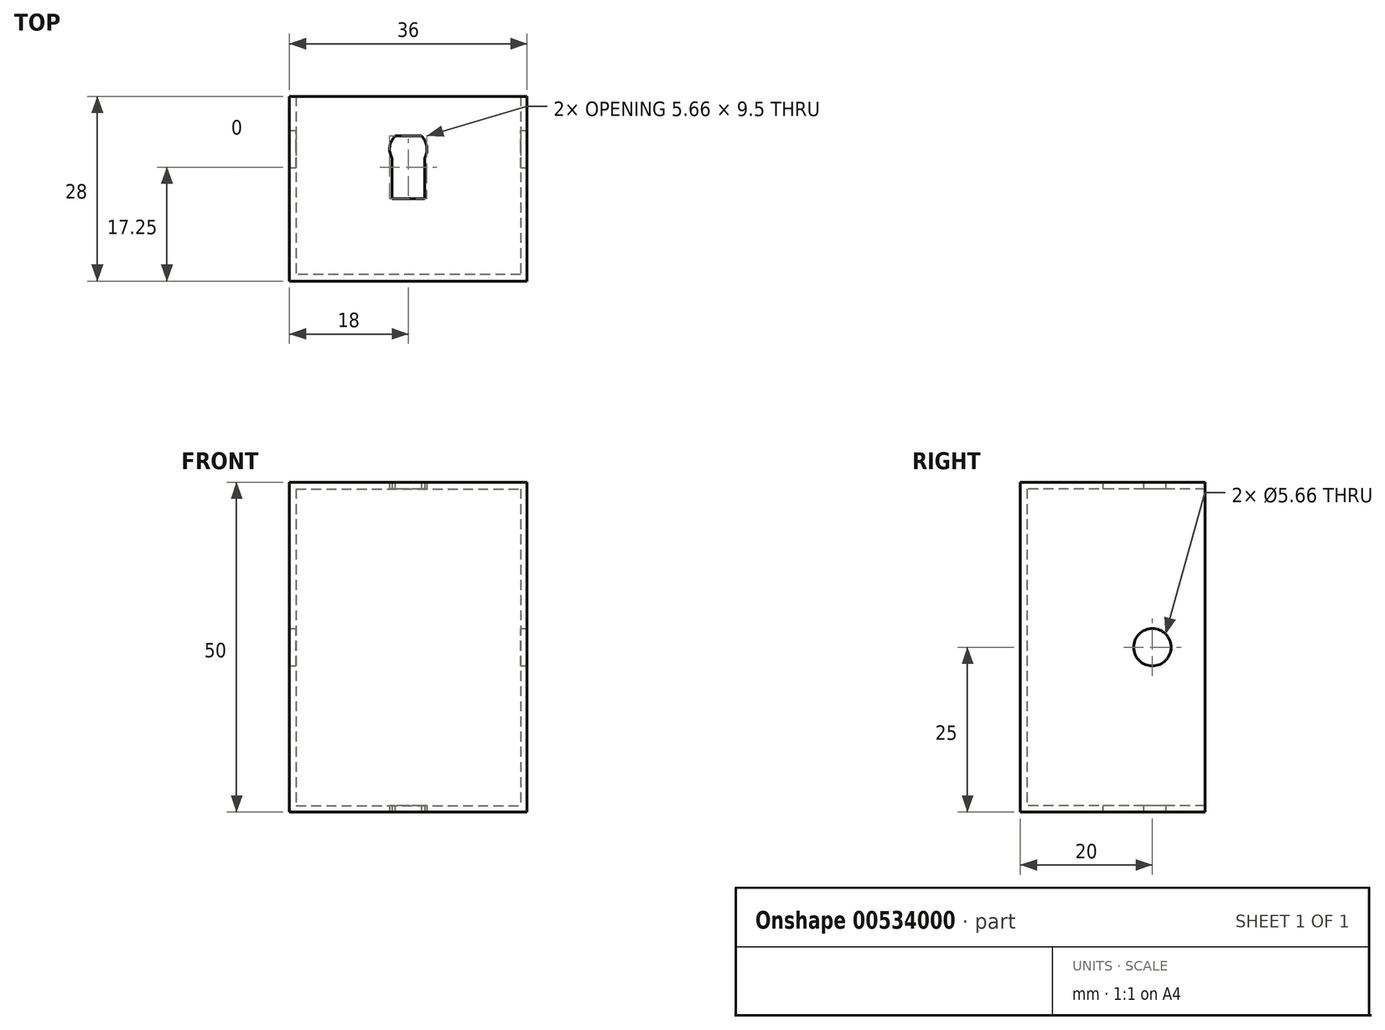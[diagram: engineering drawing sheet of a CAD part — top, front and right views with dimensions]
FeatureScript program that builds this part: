
annotation { "Feature Type Name" : "Feature", "Feature Type Description" : "" }
export const myFeature = defineFeature(function(context is Context, id is Id, definition is map)
    precondition{}
    {
        {
            var Q0;
            Q0=qCreatedBy(makeId("Top.planeOp"),FACE);
            var sketch = newSketch(context, id + "F0", { "sketchPlane" : qUnion([Q0])});
            skCircle(sketch, "E0", {"center": v(0, 0) * mm, "radius": 15 * mm});
            skLineSegment(sketch, "E1", {"start": v(0, 15) * mm, "end": v(0, -15) * mm});
            skLineSegment(sketch, "E2.bottom", {"start": v(2.5, 7.5) * mm, "end": v(-2.5, 7.5) * mm});
            skLineSegment(sketch, "E2.top", {"start": v(2.5, -7.5) * mm, "end": v(-2.5, -7.5) * mm});
            skLineSegment(sketch, "E2.left", {"start": v(2.5, 7.5) * mm, "end": v(2.5, -7.5) * mm});
            skLineSegment(sketch, "E2.right", {"start": v(-2.5, 7.5) * mm, "end": v(-2.5, -7.5) * mm});
            skLineSegment(sketch, "E3.bottom", {"start": v(6, 15.5) * mm, "end": v(-6, 15.5) * mm});
            skLineSegment(sketch, "E3.top", {"start": v(6, 8.5) * mm, "end": v(-6, 8.5) * mm});
            skLineSegment(sketch, "E3.left", {"start": v(6, 15.5) * mm, "end": v(6, 8.5) * mm});
            skLineSegment(sketch, "E3.right", {"start": v(-6, 15.5) * mm, "end": v(-6, 8.5) * mm});
            skPoint(sketch, "E3.middle", {"position": v(0, 12) * mm});
            skLineSegment(sketch, "E4.bottom", {"start": v(17, 19) * mm, "end": v(-17, 19) * mm});
            skLineSegment(sketch, "E4.top", {"start": v(17, -19) * mm, "end": v(-17, -19) * mm});
            skLineSegment(sketch, "E4.left", {"start": v(17, 19) * mm, "end": v(17, -19) * mm});
            skLineSegment(sketch, "E4.right", {"start": v(-17, 19) * mm, "end": v(-17, -19) * mm});
            skLineSegment(sketch, "E5.0", {"start": v(18, 20) * mm, "end": v(-18, 20) * mm});
            skLineSegment(sketch, "E5.1", {"start": v(18, 20) * mm, "end": v(18, -20) * mm});
            skLineSegment(sketch, "E5.2", {"start": v(18, -20) * mm, "end": v(-18, -20) * mm});
            skLineSegment(sketch, "E5.3", {"start": v(-18, 20) * mm, "end": v(-18, -20) * mm});
            skLineSegment(sketch, "E6", {"start": v(-18, 8) * mm, "end": v(18, 8) * mm});
            skLineSegment(sketch, "E7", {"start": v(18, 8) * mm, "end": v(17, 8) * mm});
            skLineSegment(sketch, "E8", {"start": v(-18, 8) * mm, "end": v(-17, 8) * mm});
            skCircle(sketch, "E9", {"center": v(0, 0) * mm, "radius": 17 * mm});
            skLineSegment(sketch, "E10.bottom", {"start": v(2, 2) * mm, "end": v(-2, 2) * mm});
            skLineSegment(sketch, "E10.top", {"start": v(2, -2) * mm, "end": v(-2, -2) * mm});
            skLineSegment(sketch, "E10.left", {"start": v(2, 2) * mm, "end": v(2, -2) * mm});
            skLineSegment(sketch, "E10.right", {"start": v(-2, 2) * mm, "end": v(-2, -2) * mm});
            skCircle(sketch, "E11", {"center": v(0, 0) * mm, "radius": 2.83 * mm});
            skLineSegment(sketch, "E12", {"start": v(2, 0) * mm, "end": v(-2, 0) * mm});
            skLineSegment(sketch, "E13", {"start": v(-18, 0) * mm, "end": v(18, 0) * mm, "construction": true});
            skSolve(sketch);
        }
        {
            var Q0;
            Q0=qCreatedBy(makeId("Right.planeOp"),FACE);
            var sketch = newSketch(context, id + "F1", { "sketchPlane" : qUnion([Q0])});
            skLineSegment(sketch, "E14.bottom", {"start": v(2, 2) * mm, "end": v(-2, 2) * mm});
            skLineSegment(sketch, "E14.top", {"start": v(2, -2) * mm, "end": v(-2, -2) * mm});
            skLineSegment(sketch, "E14.left", {"start": v(2, 2) * mm, "end": v(2, -2) * mm});
            skLineSegment(sketch, "E14.right", {"start": v(-2, 2) * mm, "end": v(-2, -2) * mm});
            skPoint(sketch, "E14.middle", {"position": v(0, 0) * mm});
            skCircle(sketch, "E15", {"center": v(0, 0) * mm, "radius": 2.83 * mm});
            skSolve(sketch);
        }
        {
            var Q0;
            {var subQ1=sQuery(id+"F0.wireOp",EDGE,"E4.top");Q0=makeQuery(id+"F0.imprint","IMPRINT",FACE,{"disambiguationData":[TD([[makeQuery(id+"F0.imprint","IMPRINT",EDGE,{"derivedFrom":subQ1}),1.0]])]});}
            extrude(context, id + "F2", {"entities" : qUnion([Q0]), "depth" : 25 * mm, "offsetDistance" : 25 * mm, "hasSecondDirection" : true, "secondDirectionOppositeDirection" : true, "secondDirectionDepth" : 25 * mm});
        }
        {
            var Q0;
            {var subQ1=sQuery(id+"F0.wireOp",EDGE,"E4.top");Q0=makeQuery(id+"F0.imprint","IMPRINT",FACE,{"disambiguationData":[TD([[makeQuery(id+"F0.imprint","IMPRINT",EDGE,{"derivedFrom":subQ1}),-1.0]])]});}
            var Q1;
            {var subQ1=sQuery(id+"F0.wireOp",EDGE,"E0");var subQ5=makeQuery(id+"F0.imprint","INTERSECT",VERTEX,{"disambiguationData":[OD(1.0)],"derivedFrom":[subQ1,sQuery(id+"F0.wireOp",EDGE,"E1")]});Q1=makeQuery(id+"F0.imprint","IMPRINT",FACE,{"disambiguationData":[TD([[makeQuery(id+"F0.imprint","IMPRINT",EDGE,{"disambiguationData":[TD([[subQ5,1.0]])],"derivedFrom":subQ1}),-1.0]])]});}
            var Q2;
            {var subQ0=sQuery(id+"F0.wireOp",EDGE,"E2.right");Q2=makeQuery(id+"F0.imprint","IMPRINT",FACE,{"disambiguationData":[TD([[makeQuery(id+"F0.imprint","IMPRINT",EDGE,{"derivedFrom":subQ0}),-1.0]])]});}
            var Q3;
            {var subQ0=sQuery(id+"F0.wireOp",EDGE,"E2.left");Q3=makeQuery(id+"F0.imprint","IMPRINT",FACE,{"disambiguationData":[TD([[makeQuery(id+"F0.imprint","IMPRINT",EDGE,{"derivedFrom":subQ0}),1.0]])]});}
            var Q4;
            {var subQ1=sQuery(id+"F0.wireOp",EDGE,"E4.right");var subQ3=sQuery(id+"F0.wireOp",EDGE,"E9");var subQ4=makeQuery(id+"F0.imprint","INTERSECT",VERTEX,{"derivedFrom":[subQ1,subQ3]});Q4=makeQuery(id+"F0.imprint","IMPRINT",FACE,{"disambiguationData":[TD([[makeQuery(id+"F0.imprint","IMPRINT",EDGE,{"disambiguationData":[TD([[subQ4,1.0]])],"derivedFrom":subQ3}),-1.0]])]});}
            var Q5;
            {var subQ1=sQuery(id+"F0.wireOp",EDGE,"E4.left");var subQ3=sQuery(id+"F0.wireOp",EDGE,"E9");var subQ4=makeQuery(id+"F0.imprint","INTERSECT",VERTEX,{"derivedFrom":[subQ1,subQ3]});Q5=makeQuery(id+"F0.imprint","IMPRINT",FACE,{"disambiguationData":[TD([[makeQuery(id+"F0.imprint","IMPRINT",EDGE,{"disambiguationData":[TD([[subQ4,-1.0]])],"derivedFrom":subQ3}),-1.0]])]});}
            var Q6;
            {var subQ1=sQuery(id+"F0.wireOp",EDGE,"E2.bottom");var subQ6=sQuery(id+"F0.wireOp",EDGE,"E1");var subQ8=makeQuery(id+"F0.imprint","INTERSECT",VERTEX,{"derivedFrom":[subQ6,subQ1]});Q6=makeQuery(id+"F0.imprint","IMPRINT",FACE,{"disambiguationData":[TD([[makeQuery(id+"F0.imprint","IMPRINT",EDGE,{"disambiguationData":[TD([[subQ8,-1.0]])],"derivedFrom":subQ6}),-1.0]])]});}
            var Q7;
            {var subQ1=sQuery(id+"F0.wireOp",EDGE,"E2.bottom");var subQ3=sQuery(id+"F0.wireOp",EDGE,"E1");var subQ4=makeQuery(id+"F0.imprint","INTERSECT",VERTEX,{"derivedFrom":[subQ3,subQ1]});Q7=makeQuery(id+"F0.imprint","IMPRINT",FACE,{"disambiguationData":[TD([[makeQuery(id+"F0.imprint","IMPRINT",EDGE,{"disambiguationData":[TD([[subQ4,-1.0]])],"derivedFrom":subQ3}),1.0]])]});}
            var Q8;
            {var subQ0=sQuery(id+"F0.wireOp",EDGE,"E11");var subQ2=sQuery(id+"F0.wireOp",EDGE,"E1");var subQ3=makeQuery(id+"F0.imprint","INTERSECT",VERTEX,{"disambiguationData":[OD(1.0)],"derivedFrom":[subQ2,subQ0]});Q8=makeQuery(id+"F0.imprint","IMPRINT",FACE,{"disambiguationData":[TD([[makeQuery(id+"F0.imprint","IMPRINT",EDGE,{"disambiguationData":[TD([[subQ3,-1.0]])],"derivedFrom":subQ2}),1.0]])]});}
            var Q9;
            {var subQ0=sQuery(id+"F0.wireOp",EDGE,"E11");var subQ6=sQuery(id+"F0.wireOp",EDGE,"E1");var subQ7=makeQuery(id+"F0.imprint","INTERSECT",VERTEX,{"disambiguationData":[OD(1.0)],"derivedFrom":[subQ6,subQ0]});Q9=makeQuery(id+"F0.imprint","IMPRINT",FACE,{"disambiguationData":[TD([[makeQuery(id+"F0.imprint","IMPRINT",EDGE,{"disambiguationData":[TD([[subQ7,-1.0]])],"derivedFrom":subQ6}),-1.0]])]});}
            extrude(context, id + "F3", {"entities" : qUnion([Q0, Q1, Q2, Q3, Q4, Q5, Q6, Q7, Q8, Q9]), "operationType" : NewBodyOperationType.ADD, "depth" : 25 * mm, "offsetDistance" : 25 * mm, "hasSecondDirection" : true, "secondDirectionOppositeDirection" : true, "secondDirectionDepth" : 25 * mm});
        }
        {
            var Q0;
            {var subQ1=sQuery(id+"F0.wireOp",EDGE,"E4.top");Q0=makeQuery(id+"F0.imprint","IMPRINT",FACE,{"disambiguationData":[TD([[makeQuery(id+"F0.imprint","IMPRINT",EDGE,{"derivedFrom":subQ1}),-1.0]])]});}
            var Q1;
            {var subQ0=sQuery(id+"F0.wireOp",EDGE,"E2.left");Q1=makeQuery(id+"F0.imprint","IMPRINT",FACE,{"disambiguationData":[TD([[makeQuery(id+"F0.imprint","IMPRINT",EDGE,{"derivedFrom":subQ0}),1.0]])]});}
            var Q2;
            {var subQ1=sQuery(id+"F0.wireOp",EDGE,"E0");var subQ5=makeQuery(id+"F0.imprint","INTERSECT",VERTEX,{"disambiguationData":[OD(1.0)],"derivedFrom":[subQ1,sQuery(id+"F0.wireOp",EDGE,"E1")]});Q2=makeQuery(id+"F0.imprint","IMPRINT",FACE,{"disambiguationData":[TD([[makeQuery(id+"F0.imprint","IMPRINT",EDGE,{"disambiguationData":[TD([[subQ5,1.0]])],"derivedFrom":subQ1}),-1.0]])]});}
            var Q3;
            {var subQ0=sQuery(id+"F0.wireOp",EDGE,"E2.right");Q3=makeQuery(id+"F0.imprint","IMPRINT",FACE,{"disambiguationData":[TD([[makeQuery(id+"F0.imprint","IMPRINT",EDGE,{"derivedFrom":subQ0}),-1.0]])]});}
            var Q4;
            {var subQ1=sQuery(id+"F0.wireOp",EDGE,"E4.right");var subQ3=sQuery(id+"F0.wireOp",EDGE,"E9");var subQ4=makeQuery(id+"F0.imprint","INTERSECT",VERTEX,{"derivedFrom":[subQ1,subQ3]});Q4=makeQuery(id+"F0.imprint","IMPRINT",FACE,{"disambiguationData":[TD([[makeQuery(id+"F0.imprint","IMPRINT",EDGE,{"disambiguationData":[TD([[subQ4,1.0]])],"derivedFrom":subQ3}),-1.0]])]});}
            var Q5;
            {var subQ1=sQuery(id+"F0.wireOp",EDGE,"E4.left");var subQ3=sQuery(id+"F0.wireOp",EDGE,"E9");var subQ4=makeQuery(id+"F0.imprint","INTERSECT",VERTEX,{"derivedFrom":[subQ1,subQ3]});Q5=makeQuery(id+"F0.imprint","IMPRINT",FACE,{"disambiguationData":[TD([[makeQuery(id+"F0.imprint","IMPRINT",EDGE,{"disambiguationData":[TD([[subQ4,-1.0]])],"derivedFrom":subQ3}),-1.0]])]});}
            var Q6;
            {var subQ0=sQuery(id+"F0.wireOp",EDGE,"E11");var subQ6=sQuery(id+"F0.wireOp",EDGE,"E1");var subQ7=makeQuery(id+"F0.imprint","INTERSECT",VERTEX,{"disambiguationData":[OD(1.0)],"derivedFrom":[subQ6,subQ0]});Q6=makeQuery(id+"F0.imprint","IMPRINT",FACE,{"disambiguationData":[TD([[makeQuery(id+"F0.imprint","IMPRINT",EDGE,{"disambiguationData":[TD([[subQ7,-1.0]])],"derivedFrom":subQ6}),-1.0]])]});}
            var Q7;
            {var subQ0=sQuery(id+"F0.wireOp",EDGE,"E11");var subQ2=sQuery(id+"F0.wireOp",EDGE,"E1");var subQ3=makeQuery(id+"F0.imprint","INTERSECT",VERTEX,{"disambiguationData":[OD(1.0)],"derivedFrom":[subQ2,subQ0]});Q7=makeQuery(id+"F0.imprint","IMPRINT",FACE,{"disambiguationData":[TD([[makeQuery(id+"F0.imprint","IMPRINT",EDGE,{"disambiguationData":[TD([[subQ3,-1.0]])],"derivedFrom":subQ2}),1.0]])]});}
            var Q8;
            {var subQ1=sQuery(id+"F0.wireOp",EDGE,"E2.bottom");var subQ6=sQuery(id+"F0.wireOp",EDGE,"E1");var subQ8=makeQuery(id+"F0.imprint","INTERSECT",VERTEX,{"derivedFrom":[subQ6,subQ1]});Q8=makeQuery(id+"F0.imprint","IMPRINT",FACE,{"disambiguationData":[TD([[makeQuery(id+"F0.imprint","IMPRINT",EDGE,{"disambiguationData":[TD([[subQ8,-1.0]])],"derivedFrom":subQ6}),-1.0]])]});}
            var Q9;
            {var subQ1=sQuery(id+"F0.wireOp",EDGE,"E2.bottom");var subQ3=sQuery(id+"F0.wireOp",EDGE,"E1");var subQ4=makeQuery(id+"F0.imprint","INTERSECT",VERTEX,{"derivedFrom":[subQ3,subQ1]});Q9=makeQuery(id+"F0.imprint","IMPRINT",FACE,{"disambiguationData":[TD([[makeQuery(id+"F0.imprint","IMPRINT",EDGE,{"disambiguationData":[TD([[subQ4,-1.0]])],"derivedFrom":subQ3}),1.0]])]});}
            extrude(context, id + "F4", {"entities" : qUnion([Q0, Q1, Q2, Q3, Q4, Q5, Q6, Q7, Q8, Q9]), "operationType" : NewBodyOperationType.REMOVE, "depth" : 24 * mm, "offsetDistance" : 25 * mm, "hasSecondDirection" : true, "secondDirectionOppositeDirection" : true, "secondDirectionDepth" : 24 * mm});
        }
        {
            var Q0;
            {var subQ0=sQuery(id+"F1.wireOp",EDGE,"E14.top");Q0=makeQuery(id+"F1.imprint","IMPRINT",FACE,{"disambiguationData":[TD([[makeQuery(id+"F1.imprint","IMPRINT",EDGE,{"derivedFrom":subQ0}),1.0]])]});}
            var Q1;
            Q1=makeQuery(id+"F1.imprint","IMPRINT",FACE,{"disambiguationData":[TD([[makeQuery(id+"F1.imprint","IMPRINT",EDGE,{"derivedFrom":sQuery(id+"F1.wireOp",EDGE,"E14.bottom")}),1.0]])]});
            var Q2;
            {var subQ0=sQuery(id+"F1.wireOp",EDGE,"E14.bottom");Q2=makeQuery(id+"F1.imprint","IMPRINT",FACE,{"disambiguationData":[TD([[makeQuery(id+"F1.imprint","IMPRINT",EDGE,{"derivedFrom":subQ0}),-1.0]])]});}
            var Q3;
            {var subQ0=sQuery(id+"F1.wireOp",EDGE,"E14.left");Q3=makeQuery(id+"F1.imprint","IMPRINT",FACE,{"disambiguationData":[TD([[makeQuery(id+"F1.imprint","IMPRINT",EDGE,{"derivedFrom":subQ0}),1.0]])]});}
            var Q4;
            {var subQ0=sQuery(id+"F1.wireOp",EDGE,"E14.right");Q4=makeQuery(id+"F1.imprint","IMPRINT",FACE,{"disambiguationData":[TD([[makeQuery(id+"F1.imprint","IMPRINT",EDGE,{"derivedFrom":subQ0}),-1.0]])]});}
            extrude(context, id + "F5", {"entities" : qUnion([Q0, Q1, Q2, Q3, Q4]), "operationType" : NewBodyOperationType.REMOVE, "oppositeDirection" : true, "depth" : 25 * mm, "offsetDistance" : 25 * mm, "hasSecondDirection" : true, "secondDirectionOppositeDirection" : false, "secondDirectionDepth" : 25 * mm});
        }
    });
